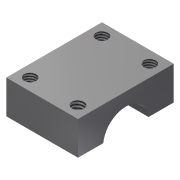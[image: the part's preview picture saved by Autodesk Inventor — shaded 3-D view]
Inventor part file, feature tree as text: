
AUTODESK INVENTOR PART (.ipt)
format: ipt  version: 2015 (Build 190159000, 159)  size: 124,928 bytes
history: native  units: mm
features: hole x5, extrude x1, sketch x1
ambient origin geometry x8: Origin, YZ Plane, XZ Plane, XY Plane, X Axis, Y Axis, Z Axis, Center Point
bodies: Body1 (feature_tree)
feature tree (7):
  extrude  "Extrusion2"  Depth=40.0mm
  hole  "Hole3"  [1 undecoded]
  hole  "Hole4"  [1 undecoded]
  hole  "Hole5"  [1 undecoded]
  hole  "Hole6"  [1 undecoded]
  hole  "Hole7"  [1 undecoded]
  sketch  "Sketch4"  dims[d37=30.0mm d38=40.0mm d39=14.0mm d40=0.0mm d50=5.0mm d51=5.0mm d52=4.917mm d53=12.0mm d54=9.0mm d55=8.0mm d56=90.0deg d57=17.1mm d58=20.594885mm d59=5.0mm d60=5.0mm d61=4.917mm d62=12.0mm d63=9.0mm d64=8.0mm d65=90.0deg d66=17.1mm d67=20.594885mm d68=5.0mm d69=5.0mm d70=4.978mm d71=12.7mm d72=9.0mm d73=8.0mm d74=90.0deg d75=19.05mm d76=20.594885mm d77=5.0mm d78=5.0mm d79=4.917mm d80=12.0mm d81=9.0mm d82=8.0mm d83=90.0deg d84=17.1mm d85=20.594885mm d86=15.0mm d87=20.0mm d88=19.0mm d89=6.0mm d90=4.0mm d91=2.0mm d92=90.0deg d93=8.0mm d94=20.594885mm]
note: 5 required parameter values undecoded (feature->parameter linkage not recoverable at this tier; creation-order binding heuristic only, values carry confidence <= 0.55)
